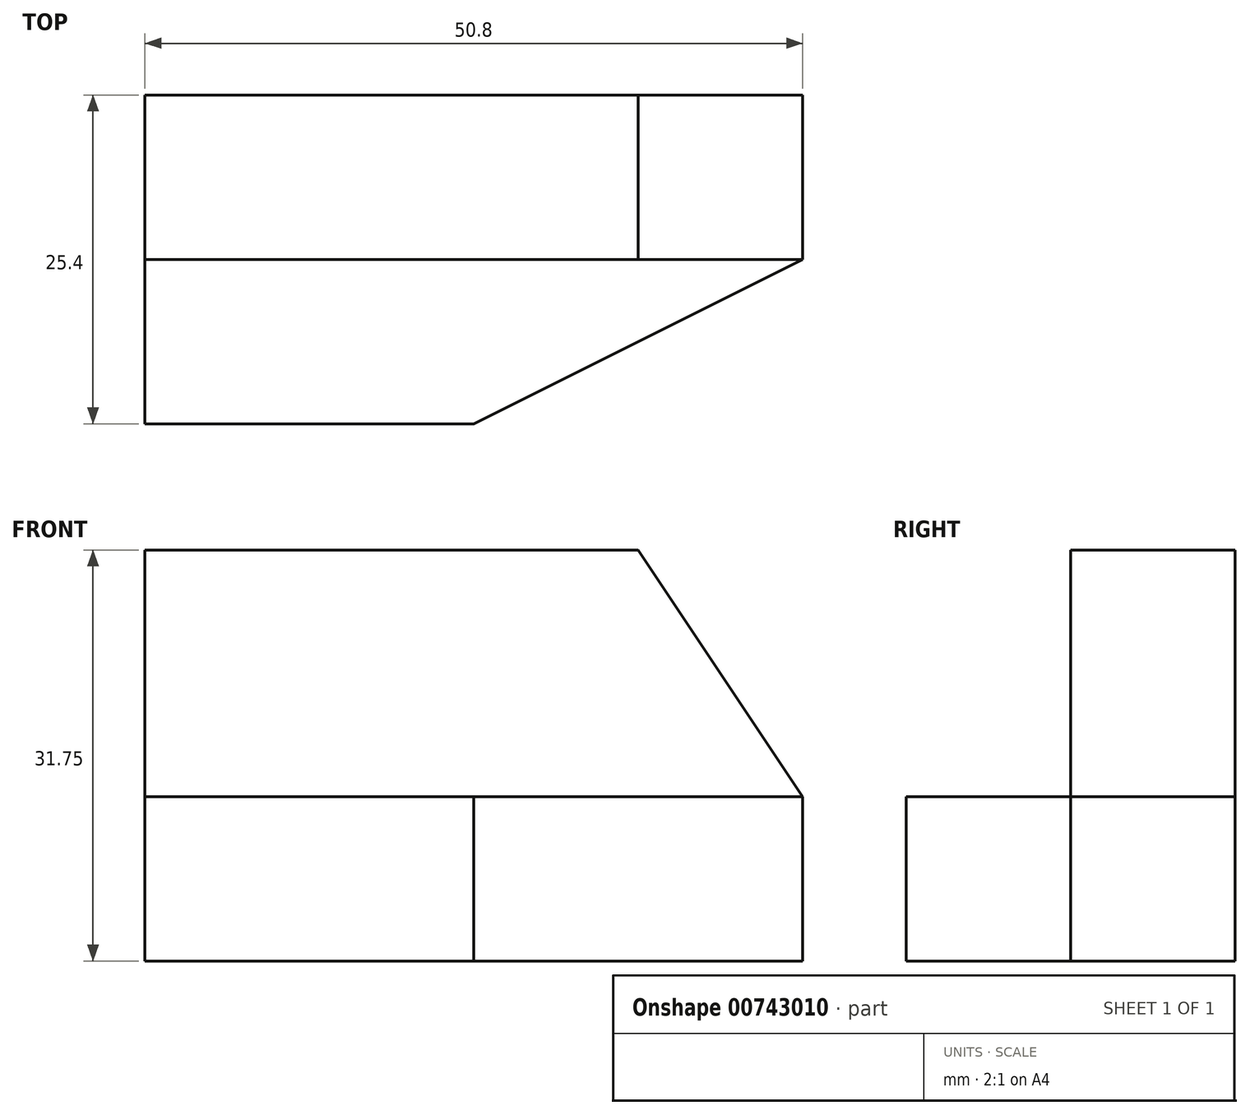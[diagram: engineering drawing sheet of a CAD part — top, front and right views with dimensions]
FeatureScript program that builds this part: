
annotation { "Feature Type Name" : "Feature", "Feature Type Description" : "" }
export const myFeature = defineFeature(function(context is Context, id is Id, definition is map)
    precondition{}
    {
        {
            var Q0;
            Q0=qCreatedBy(makeId("Front.planeOp"),FACE);
            var sketch = newSketch(context, id + "F0", { "sketchPlane" : qUnion([Q0])});
            skLineSegment(sketch, "E0", {"start": v(0, 0) * mm, "end": v(50.8, 0) * mm});
            skLineSegment(sketch, "E1", {"start": v(50.8, 0) * mm, "end": v(50.8, 31.75) * mm});
            skLineSegment(sketch, "E2", {"start": v(50.8, 31.75) * mm, "end": v(0, 31.75) * mm});
            skLineSegment(sketch, "E3", {"start": v(0, 31.75) * mm, "end": v(0, 0) * mm});
            skSolve(sketch);
        }
        {
            var Q0;
            Q0=makeQuery(id+"F0.imprint","IMPRINT",FACE,{"disambiguationData":[TD([[makeQuery(id+"F0.imprint","IMPRINT",EDGE,{"derivedFrom":sQuery(id+"F0.wireOp",EDGE,"E0")}),1.0]])]});
            extrude(context, id + "F1", {"entities" : qUnion([Q0]), "depth" : 25.4 * mm, "offsetDistance" : 25.4 * mm});
        }
        {
            var Q0;
            Q0=makeQuery(id+"F1.opExtrude","CAP_FACE",FACE,{"disambiguationData":[OSD([sQuery(id+"F0.wireOp",EDGE,"E0"),sQuery(id+"F0.wireOp",EDGE,"E1"),sQuery(id+"F0.wireOp",EDGE,"E2"),sQuery(id+"F0.wireOp",EDGE,"E3")])],"isStart":false});
            var sketch = newSketch(context, id + "F2", { "sketchPlane" : qUnion([Q0])});
            skLineSegment(sketch, "E4", {"start": v(0, 12.7) * mm, "end": v(50.8, 12.7) * mm});
            skSolve(sketch);
        }
        {
            var Q0;
            {var subQ0=sQuery(id+"F2.wireOp",EDGE,"E4");Q0=makeQuery(id+"F2.imprint","IMPRINT",FACE,{"disambiguationData":[TD([[makeQuery(id+"F2.imprint","IMPRINT",EDGE,{"derivedFrom":subQ0}),1.0]])]});}
            extrude(context, id + "F3", {"entities" : qUnion([Q0]), "operationType" : NewBodyOperationType.REMOVE, "oppositeDirection" : true, "depth" : 12.7 * mm, "offsetDistance" : 25.4 * mm});
        }
        {
            var Q0;
            Q0=makeQuery(id+"F3.boolean.opBoolean","COPY",FACE,{"derivedFrom":makeQuery(id+"F3.opExtrude","SWEPT_FACE",FACE,{"disambiguationData":[OSD([sQuery(id+"F2.wireOp",EDGE,"E4")])]})});
            var sketch = newSketch(context, id + "F4", { "sketchPlane" : qUnion([Q0])});
            skLineSegment(sketch, "E5", {"start": v(50.8, -12.7) * mm, "end": v(25.4, -25.4) * mm});
            skSolve(sketch);
        }
        {
            var Q0;
            {var subQ0=sQuery(id+"F4.wireOp",EDGE,"E5");Q0=makeQuery(id+"F4.imprint","IMPRINT",FACE,{"disambiguationData":[TD([[makeQuery(id+"F4.imprint","IMPRINT",EDGE,{"derivedFrom":subQ0}),1.0]])]});}
            extrude(context, id + "F5", {"entities" : qUnion([Q0]), "operationType" : NewBodyOperationType.REMOVE, "oppositeDirection" : true, "depth" : 25.4 * mm, "offsetDistance" : 25.4 * mm});
        }
        {
            var Q0;
            Q0=makeQuery(id+"F3.boolean.opBoolean","COPY",FACE,{"derivedFrom":makeQuery(id+"F3.opExtrude","CAP_FACE",FACE,{"disambiguationData":[OSD([sQuery(id+"F0.wireOp",EDGE,"E1"),sQuery(id+"F0.wireOp",EDGE,"E2"),sQuery(id+"F0.wireOp",EDGE,"E3"),sQuery(id+"F2.wireOp",EDGE,"E4")])],"isStart":false})});
            var sketch = newSketch(context, id + "F6", { "sketchPlane" : qUnion([Q0])});
            skLineSegment(sketch, "E6", {"start": v(50.8, 12.7) * mm, "end": v(38.1, 31.75) * mm});
            skLineSegment(sketch, "E7", {"start": v(38.1, 31.75) * mm, "end": v(50.8, 31.75) * mm});
            skLineSegment(sketch, "E8", {"start": v(50.8, 31.75) * mm, "end": v(50.8, 12.7) * mm});
            skSolve(sketch);
        }
        {
            var Q0;
            Q0=makeQuery(id+"F6.imprint","IMPRINT",FACE,{"disambiguationData":[TD([[makeQuery(id+"F6.imprint","IMPRINT",EDGE,{"derivedFrom":sQuery(id+"F6.wireOp",EDGE,"E6")}),-1.0]])]});
            extrude(context, id + "F7", {"entities" : qUnion([Q0]), "operationType" : NewBodyOperationType.REMOVE, "oppositeDirection" : true, "depth" : 25.4 * mm, "offsetDistance" : 25.4 * mm});
        }
    });
